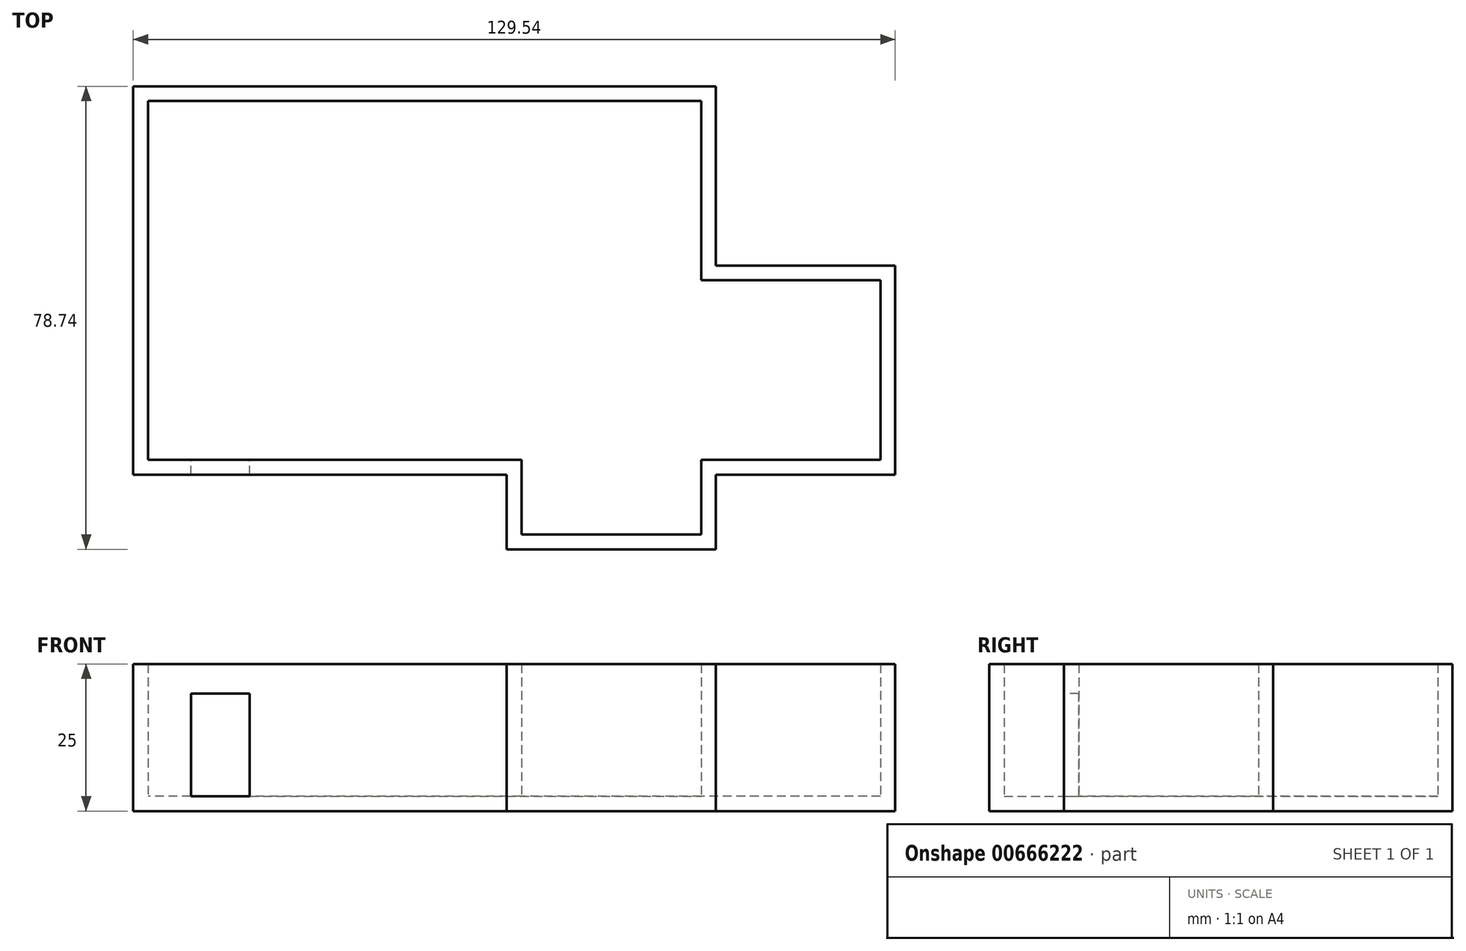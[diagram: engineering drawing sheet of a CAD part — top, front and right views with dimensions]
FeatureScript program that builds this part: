
annotation { "Feature Type Name" : "Feature", "Feature Type Description" : "" }
export const myFeature = defineFeature(function(context is Context, id is Id, definition is map)
    precondition{}
    {
        {
            var Q0;
            Q0=qCreatedBy(makeId("Top.planeOp"),FACE);
            var sketch = newSketch(context, id + "F0", { "sketchPlane" : qUnion([Q0])});
            skLineSegment(sketch, "E0", {"start": v(-73.66, -10.71) * mm, "end": v(-73.66, 55.33) * mm});
            skLineSegment(sketch, "E1", {"start": v(-73.66, 55.33) * mm, "end": v(25.4, 55.33) * mm});
            skLineSegment(sketch, "E2", {"start": v(25.4, 55.33) * mm, "end": v(25.4, 24.85) * mm});
            skLineSegment(sketch, "E3", {"start": v(25.4, 24.85) * mm, "end": v(55.88, 24.85) * mm});
            skLineSegment(sketch, "E4", {"start": v(55.88, 24.85) * mm, "end": v(55.88, -10.71) * mm});
            skLineSegment(sketch, "E5", {"start": v(55.88, -10.71) * mm, "end": v(25.4, -10.71) * mm});
            skLineSegment(sketch, "E6", {"start": v(25.4, -10.71) * mm, "end": v(25.4, -23.41) * mm});
            skLineSegment(sketch, "E7", {"start": v(25.4, -23.41) * mm, "end": v(-10.16, -23.41) * mm});
            skLineSegment(sketch, "E8", {"start": v(-10.16, -23.41) * mm, "end": v(-10.16, -10.71) * mm});
            skLineSegment(sketch, "E9", {"start": v(-10.16, -10.71) * mm, "end": v(-73.66, -10.71) * mm});
            skSolve(sketch);
        }
        {
            var Q0;
            Q0=makeQuery(id+"F0.imprint","IMPRINT",FACE,{"disambiguationData":[TD([[makeQuery(id+"F0.imprint","IMPRINT",EDGE,{"derivedFrom":sQuery(id+"F0.wireOp",EDGE,"E0")}),-1.0]])]});
            extrude(context, id + "F1", {"entities" : qUnion([Q0]), "depth" : 25 * mm, "offsetDistance" : 25 * mm});
        }
        {
            var Q0;
            Q0=makeQuery(id+"F1.opExtrude","CAP_FACE",FACE,{"disambiguationData":[OSD([sQuery(id+"F0.wireOp",EDGE,"E0"),sQuery(id+"F0.wireOp",EDGE,"E1"),sQuery(id+"F0.wireOp",EDGE,"E2"),sQuery(id+"F0.wireOp",EDGE,"E3"),sQuery(id+"F0.wireOp",EDGE,"E4"),sQuery(id+"F0.wireOp",EDGE,"E5"),sQuery(id+"F0.wireOp",EDGE,"E6"),sQuery(id+"F0.wireOp",EDGE,"E7"),sQuery(id+"F0.wireOp",EDGE,"E8"),sQuery(id+"F0.wireOp",EDGE,"E9")])],"isStart":false});
            shell(context, id + "F2", {"entities" : qUnion([Q0]), "thickness" : 2.5 * mm});
        }
        {
            var Q0;
            Q0=makeQuery(id+"F1.opExtrude","SWEPT_FACE",FACE,{"disambiguationData":[OSD([sQuery(id+"F0.wireOp",EDGE,"E9")])]});
            var sketch = newSketch(context, id + "F3", { "sketchPlane" : qUnion([Q0])});
            skLineSegment(sketch, "E10", {"start": v(-63.86, 0) * mm, "end": v(-63.86, 20) * mm});
            skLineSegment(sketch, "E11", {"start": v(-63.86, 20) * mm, "end": v(-53.86, 20) * mm});
            skLineSegment(sketch, "E12", {"start": v(-53.86, 20) * mm, "end": v(-53.86, 0) * mm});
            skLineSegment(sketch, "E13", {"start": v(-63.86, 0) * mm, "end": v(-53.86, 0) * mm});
            skSolve(sketch);
        }
        {
            var Q0;
            Q0=makeQuery(id+"F3.imprint","IMPRINT",FACE,{"disambiguationData":[TD([[makeQuery(id+"F3.imprint","IMPRINT",EDGE,{"derivedFrom":sQuery(id+"F3.wireOp",EDGE,"E10")}),-1.0]])]});
            extrude(context, id + "F4", {"entities" : qUnion([Q0]), "operationType" : NewBodyOperationType.REMOVE, "oppositeDirection" : true, "depth" : 2.5 * mm, "offsetDistance" : 25 * mm});
        }
        {
            var Q0;
            Q0=makeQuery(id+"F4.boolean.opBoolean","COPY",FACE,{"derivedFrom":makeQuery(id+"F4.opExtrude","CAP_FACE",FACE,{"disambiguationData":[OSD([sQuery(id+"F3.wireOp",EDGE,"E10"),sQuery(id+"F3.wireOp",EDGE,"E11"),sQuery(id+"F3.wireOp",EDGE,"E12"),sQuery(id+"F3.wireOp",EDGE,"E13")])],"isStart":false})});
            extrude(context, id + "F5", {"entities" : qUnion([Q0]), "operationType" : NewBodyOperationType.ADD, "depth" : 2.5 * mm, "offsetDistance" : 25 * mm});
        }
    });
